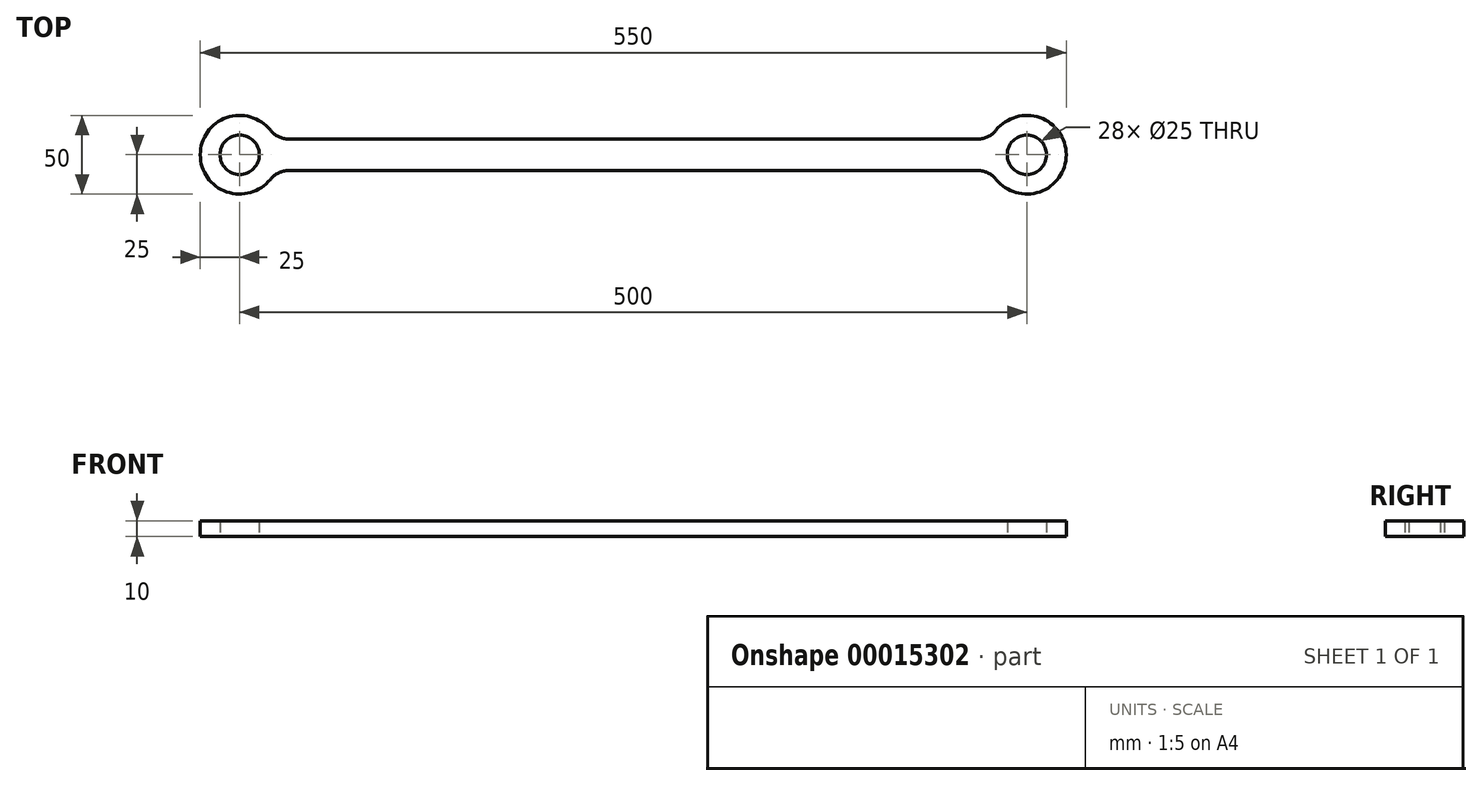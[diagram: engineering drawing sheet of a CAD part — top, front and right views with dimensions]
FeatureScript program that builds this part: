
annotation { "Feature Type Name" : "Feature", "Feature Type Description" : "" }
export const myFeature = defineFeature(function(context is Context, id is Id, definition is map)
    precondition{}
    {
        {
            var Q0;
            Q0=qCreatedBy(makeId("Top.planeOp"),FACE);
            var sketch = newSketch(context, id + "F0", { "sketchPlane" : qUnion([Q0])});
            skArc(sketch, "E0", {"start": v(19.52, 15.63) * mm, "mid": v(-25, 0) * mm, "end": v(19.52, -15.63) * mm});
            skArc(sketch, "E1", {"start": v(480.48, -15.63) * mm, "mid": v(525, 0) * mm, "end": v(480.48, 15.63) * mm});
            skLineSegment(sketch, "E2", {"start": v(31.22, 10) * mm, "end": v(468.78, 10) * mm});
            skLineSegment(sketch, "E3", {"start": v(0, 0) * mm, "end": v(500, 0) * mm, "construction": true});
            skLineSegment(sketch, "E4.MirrorCS", {"start": v(31.22, -10) * mm, "end": v(468.78, -10) * mm});
            skPoint(sketch, "E5.visualSharp", {"position": v(22.91, 10) * mm});
            skArc(sketch, "E5.filletArc", {"start": v(19.52, 15.62) * mm, "mid": v(24.73, 11.48) * mm, "end": v(31.22, 10) * mm});
            skPoint(sketch, "E6.visualSharp", {"position": v(22.91, -10) * mm});
            skArc(sketch, "E6.filletArc", {"start": v(31.22, -10) * mm, "mid": v(24.73, -11.48) * mm, "end": v(19.52, -15.62) * mm});
            skPoint(sketch, "E7.visualSharp", {"position": v(477.09, -10) * mm});
            skArc(sketch, "E7.filletArc", {"start": v(480.48, -15.63) * mm, "mid": v(475.27, -11.48) * mm, "end": v(468.78, -10) * mm});
            skPoint(sketch, "E8.visualSharp", {"position": v(477.09, 10) * mm});
            skArc(sketch, "E8.filletArc", {"start": v(468.78, 10) * mm, "mid": v(475.27, 11.48) * mm, "end": v(480.48, 15.63) * mm});
            skCircle(sketch, "E9", {"center": v(0, 0) * mm, "radius": 12.5 * mm});
            skCircle(sketch, "E10", {"center": v(500, 0) * mm, "radius": 12.5 * mm});
            skSolve(sketch);
        }
        {
            var Q0;
            Q0=qSketchRegion(id+"F0",true);
            extrude(context, id + "F1", {"entities" : qUnion([Q0]), "depth" : 10 * mm});
        }
    });
